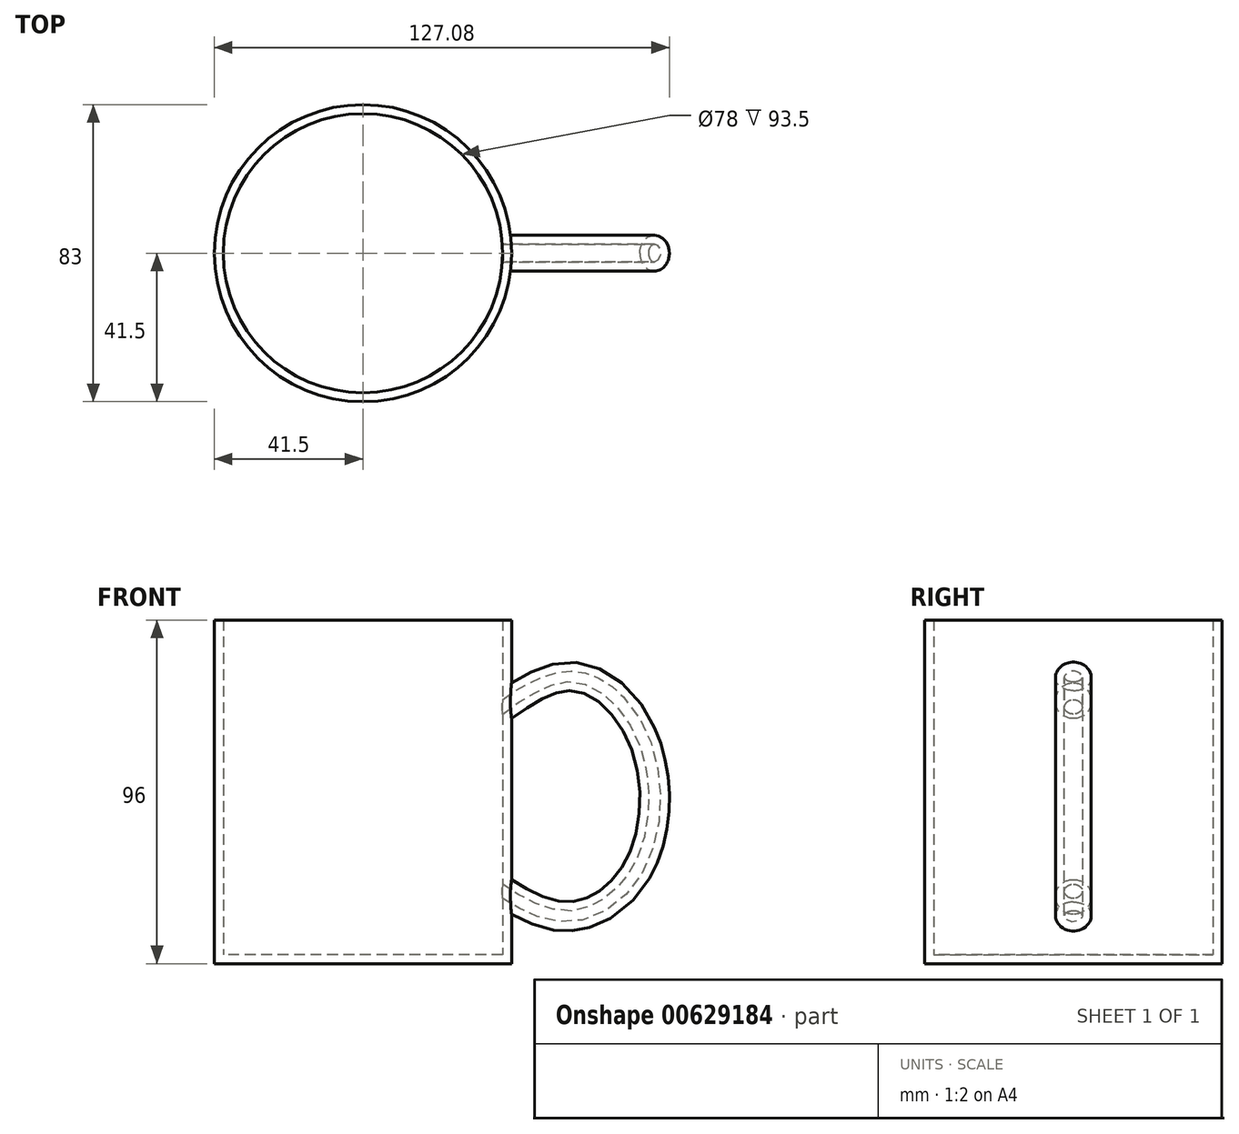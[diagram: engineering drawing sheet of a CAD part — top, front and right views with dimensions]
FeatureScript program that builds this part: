
annotation { "Feature Type Name" : "Feature", "Feature Type Description" : "" }
export const myFeature = defineFeature(function(context is Context, id is Id, definition is map)
    precondition{}
    {
        {
            var Q0;
            Q0=qCreatedBy(makeId("Top.planeOp"),FACE);
            var sketch = newSketch(context, id + "F0", { "sketchPlane" : qUnion([Q0])});
            skCircle(sketch, "E0", {"center": v(0, 0) * mm, "radius": 41.5 * mm});
            skSolve(sketch);
        }
        {
            var Q0;
            Q0 = qSketchRegion(id + "F0", true);
            extrude(context, id + "F1", {"entities" : qUnion([Q0]), "depth" : 96 * mm, "offsetDistance" : 25 * mm});
        }
        {
            var Q0;
            Q0=qCreatedBy(makeId("Front.planeOp"),FACE);
            var sketch = newSketch(context, id + "F2", { "sketchPlane" : qUnion([Q0])});
            skFitSpline(sketch, "E1", {"points": [v(34.5, 69.34) * mm, v(58.25, 80.82) * mm, v(79.12, 62.76) * mm, v(77.43, 26.1) * mm, v(56.56, 12.55) * mm, v(34.47, 22.39) * mm], "startDerivative": vector(91.4, 71.78) * mm, "endDerivative": vector(-100.43, 73.65) * mm});
            skSolve(sketch);
        }
        {
            var Q0;
            Q0=qCreatedBy(makeId("Right.planeOp"),FACE);
            cPlane(context, id + "F3", {"entities" : qUnion([Q0]), "cplaneType" : CPlaneType.OFFSET, "offset" : 41.5 * mm, "width" : 150 * mm, "height" : 150 * mm});
        }
        {
            var Q0;
            Q0=qCreatedBy(id+"F3.planeOp",FACE);
            var sketch = newSketch(context, id + "F4", { "sketchPlane" : qUnion([Q0])});
            skCircle(sketch, "E2", {"center": v(0, 73.48) * mm, "radius": 5 * mm});
            skSolve(sketch);
        }
        {
            var Q0;
            Q0=makeQuery(id+"F4.imprint","IMPRINT",FACE,{"disambiguationData":[TD([[makeQuery(id+"F4.imprint","IMPRINT",EDGE,{"derivedFrom":sQuery(id+"F4.wireOp",EDGE,"E2")}),1.0]])]});
            var Q1;
            Q1=sQuery(id+"F4.wireOp",EDGE,"E2");
            var Q2;
            Q2=sQuery(id+"F2.wireOp",EDGE,"E1");
            sweep(context, id + "F5", {"operationType" : NewBodyOperationType.ADD, "profiles" : qUnion([Q0]), "surfaceProfiles" : qUnion([Q1]), "path" : qUnion([Q2])});
        }
        {
            var Q0;
            Q0=makeQuery(id+"F1.opExtrude","CAP_FACE",FACE,{"disambiguationData":[OSD([sQuery(id+"F0.wireOp",EDGE,"E0")])],"isStart":false});
            shell(context, id + "F6", {"entities" : qUnion([Q0]), "thickness" : 2.5 * mm});
        }
    });
